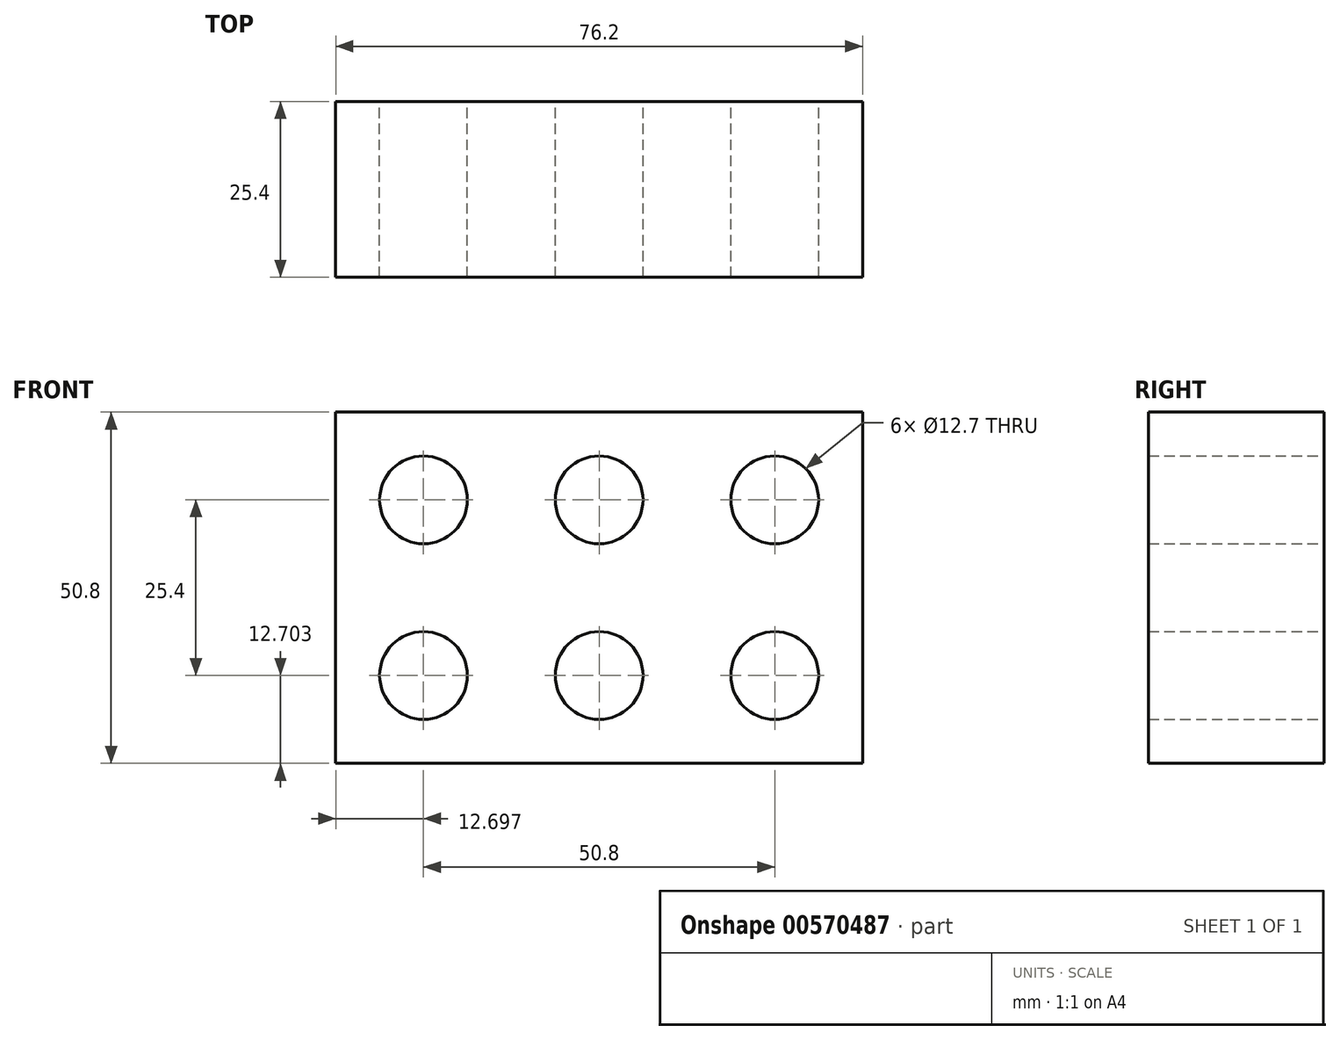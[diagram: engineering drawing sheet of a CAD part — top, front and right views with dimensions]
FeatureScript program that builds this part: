
annotation { "Feature Type Name" : "Feature", "Feature Type Description" : "" }
export const myFeature = defineFeature(function(context is Context, id is Id, definition is map)
    precondition{}
    {
        {
            var Q0;
            Q0=qCreatedBy(makeId("Front.planeOp"),FACE);
            var sketch = newSketch(context, id + "F0", { "sketchPlane" : qUnion([Q0])});
            skLineSegment(sketch, "E0.bottom", {"start": v(-14.5, -2.57) * mm, "end": v(61.7, -2.57) * mm});
            skLineSegment(sketch, "E0.top", {"start": v(-14.5, 48.23) * mm, "end": v(61.7, 48.23) * mm});
            skLineSegment(sketch, "E0.left", {"start": v(-14.5, -2.57) * mm, "end": v(-14.5, 48.23) * mm});
            skLineSegment(sketch, "E0.right", {"start": v(61.7, -2.57) * mm, "end": v(61.7, 48.23) * mm});
            skCircle(sketch, "E1", {"center": v(-1.8, 35.53) * mm, "radius": 6.35 * mm});
            skCircle(sketch, "E2", {"center": v(-1.8, 10.13) * mm, "radius": 6.35 * mm});
            skCircle(sketch, "E3.1.0.0", {"center": v(23.6, 35.53) * mm, "radius": 6.35 * mm});
            skCircle(sketch, "E3.1.0.1", {"center": v(23.6, 10.13) * mm, "radius": 6.35 * mm});
            skCircle(sketch, "E3.2.0.0", {"center": v(49, 35.53) * mm, "radius": 6.35 * mm});
            skCircle(sketch, "E3.2.0.1", {"center": v(49, 10.13) * mm, "radius": 6.35 * mm});
            skLineSegment(sketch, "E3.direction1", {"start": v(-1.8, 10.13) * mm, "end": v(23.6, 10.13) * mm, "construction": true});
            skSolve(sketch);
        }
        {
            var Q0;
            Q0=makeQuery(id+"F0.imprint","IMPRINT",FACE,{"disambiguationData":[TD([[makeQuery(id+"F0.imprint","IMPRINT",EDGE,{"derivedFrom":sQuery(id+"F0.wireOp",EDGE,"E0.bottom")}),1.0]])]});
            extrude(context, id + "F1", {"entities" : qUnion([Q0]), "endBound" : BoundingType.SYMMETRIC, "depth" : 25.4 * mm, "offsetDistance" : 25.4 * mm});
        }
    });
